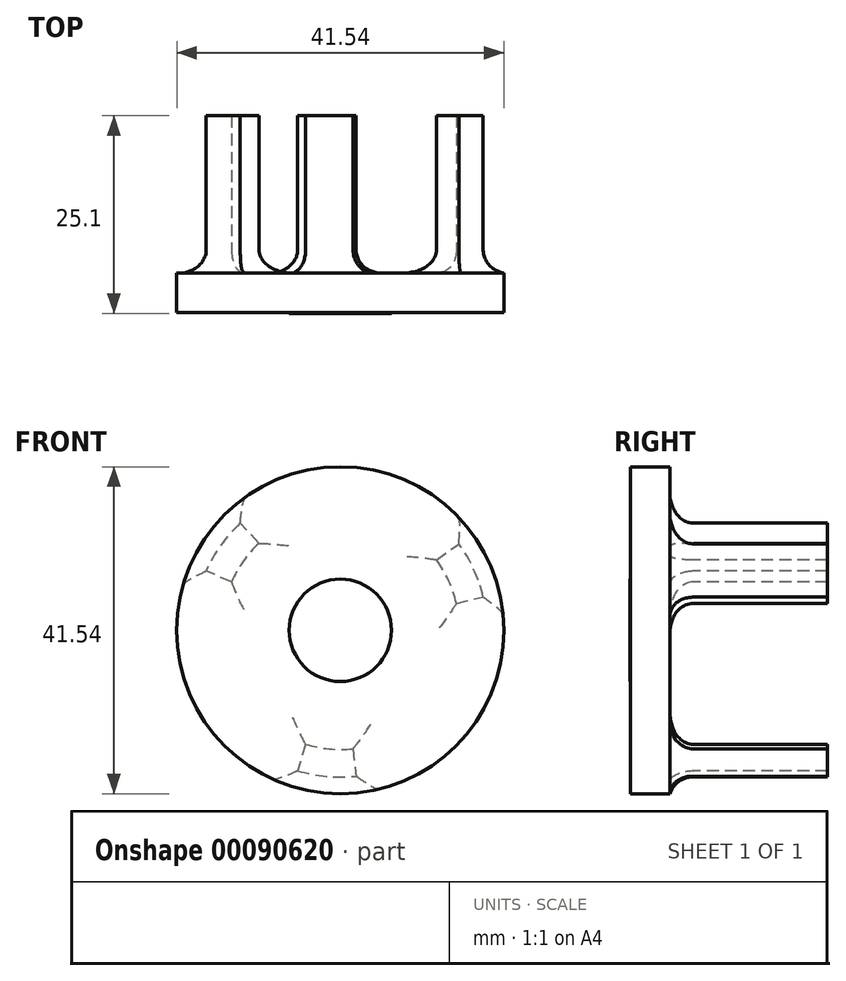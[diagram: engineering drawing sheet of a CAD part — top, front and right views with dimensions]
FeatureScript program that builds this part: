
annotation { "Feature Type Name" : "Feature", "Feature Type Description" : "" }
export const myFeature = defineFeature(function(context is Context, id is Id, definition is map)
    precondition{}
    {
        {
            var Q0;
            Q0=qCreatedBy(makeId("Front.planeOp"),FACE);
            var sketch = newSketch(context, id + "F0", { "sketchPlane" : qUnion([Q0])});
            skCircle(sketch, "E0", {"center": v(0, 0) * mm, "radius": 6.5 * mm});
            skSolve(sketch);
        }
        {
            var Q0;
            Q0=qSketchRegion(id+"F0",true);
            extrude(context, id + "F1", {"entities" : qUnion([Q0]), "depth" : .1 * mm});
        }
        {
            var Q0;
            Q0=qCreatedBy(makeId("Front.planeOp"),FACE);
            var sketch = newSketch(context, id + "F2", { "sketchPlane" : qUnion([Q0])});
            skCircle(sketch, "E1", {"center": v(0, 0) * mm, "radius": 20.77 * mm});
            skSolve(sketch);
        }
        {
            var Q0;
            Q0=makeQuery(id+"F2.imprint","IMPRINT",FACE,{"disambiguationData":[TD([[makeQuery(id+"F2.imprint","IMPRINT",EDGE,{"derivedFrom":sQuery(id+"F2.wireOp",EDGE,"E1")}),1.0]])]});
            extrude(context, id + "F3", {"entities" : qUnion([Q0]), "operationType" : NewBodyOperationType.ADD, "oppositeDirection" : true, "depth" : 5 * mm});
        }
        {
            var Q0;
            Q0=makeQuery(id+"F3.opExtrude","CAP_FACE",FACE,{"disambiguationData":[OSD([sQuery(id+"F2.wireOp",EDGE,"E1")])],"isStart":true});
            var sketch = newSketch(context, id + "F4", { "sketchPlane" : qUnion([Q0])});
            skCircle(sketch, "E2", {"center": v(0, 0) * mm, "radius": 18.64 * mm});
            skCircle(sketch, "E3", {"center": v(0, 0) * mm, "radius": 15.14 * mm});
            skLineSegment(sketch, "E4", {"start": v(0, 0) * mm, "end": v(-14.2, 15.17) * mm});
            skLineSegment(sketch, "E5", {"start": v(0, 0) * mm, "end": v(-19, 8.42) * mm});
            skLineSegment(sketch, "E6", {"start": v(0, 0) * mm, "end": v(16.79, 12.24) * mm});
            skLineSegment(sketch, "E7", {"start": v(0, 0) * mm, "end": v(20.23, 4.7) * mm});
            skLineSegment(sketch, "E8", {"start": v(0, 0) * mm, "end": v(-6.04, -19.88) * mm});
            skLineSegment(sketch, "E9", {"start": v(0, 0) * mm, "end": v(2.2, -20.66) * mm});
            skSolve(sketch);
        }
        {
            var Q0;
            {var subQ0=sQuery(id+"F4.wireOp",EDGE,"E4");var subQ1=sQuery(id+"F4.wireOp",EDGE,"E2");var subQ2=makeQuery(id+"F4.imprint","INTERSECT",VERTEX,{"derivedFrom":[subQ1,subQ0]});Q0=makeQuery(id+"F4.imprint","IMPRINT",FACE,{"disambiguationData":[TD([[makeQuery(id+"F4.imprint","IMPRINT",EDGE,{"disambiguationData":[TD([[subQ2,-1.0]])],"derivedFrom":subQ1}),1.0]])]});}
            var Q1;
            {var subQ0=sQuery(id+"F4.wireOp",EDGE,"E6");var subQ1=sQuery(id+"F4.wireOp",EDGE,"E2");var subQ2=makeQuery(id+"F4.imprint","INTERSECT",VERTEX,{"derivedFrom":[subQ1,subQ0]});Q1=makeQuery(id+"F4.imprint","IMPRINT",FACE,{"disambiguationData":[TD([[makeQuery(id+"F4.imprint","IMPRINT",EDGE,{"disambiguationData":[TD([[subQ2,1.0]])],"derivedFrom":subQ1}),1.0]])]});}
            var Q2;
            {var subQ0=sQuery(id+"F4.wireOp",EDGE,"E8");var subQ1=sQuery(id+"F4.wireOp",EDGE,"E2");var subQ2=makeQuery(id+"F4.imprint","INTERSECT",VERTEX,{"derivedFrom":[subQ1,subQ0]});Q2=makeQuery(id+"F4.imprint","IMPRINT",FACE,{"disambiguationData":[TD([[makeQuery(id+"F4.imprint","IMPRINT",EDGE,{"disambiguationData":[TD([[subQ2,-1.0]])],"derivedFrom":subQ1}),1.0]])]});}
            extrude(context, id + "F5", {"entities" : qUnion([Q0, Q1, Q2]), "operationType" : NewBodyOperationType.ADD, "oppositeDirection" : true, "depth" : 25 * mm});
        }
        {
            var Q0;
            Q0=makeQuery(id+"F5.boolean.opBoolean","INTERSECT",EDGE,{"derivedFrom":[makeQuery(id+"F3.opExtrude","CAP_FACE",FACE,{"disambiguationData":[OSD([sQuery(id+"F2.wireOp",EDGE,"E1")])],"isStart":false}),makeQuery(id+"F5.opExtrude","SWEPT_FACE",FACE,{"disambiguationData":[OSD([sQuery(id+"F4.wireOp",EDGE,"E5")])]})]});
            var Q1;
            {var subQ0=sQuery(id+"F4.wireOp",EDGE,"E3");Q1=makeQuery(id+"F5.boolean.opBoolean","INTERSECT",EDGE,{"derivedFrom":[makeQuery(id+"F3.opExtrude","CAP_FACE",FACE,{"disambiguationData":[OSD([sQuery(id+"F2.wireOp",EDGE,"E1")])],"isStart":false}),makeQuery(id+"F5.opExtrude","SWEPT_FACE",FACE,{"disambiguationData":[OSD([subQ0]),TDD([makeQuery(id+"F4.imprint","IMPRINT",EDGE,{"disambiguationData":[TD([[makeQuery(id+"F4.imprint","INTERSECT",VERTEX,{"derivedFrom":[subQ0,sQuery(id+"F4.wireOp",EDGE,"E4")]}),-1.0]])],"derivedFrom":subQ0})])]})]});}
            var Q2;
            Q2=makeQuery(id+"F5.boolean.opBoolean","INTERSECT",EDGE,{"derivedFrom":[makeQuery(id+"F3.opExtrude","CAP_FACE",FACE,{"disambiguationData":[OSD([sQuery(id+"F2.wireOp",EDGE,"E1")])],"isStart":false}),makeQuery(id+"F5.opExtrude","SWEPT_FACE",FACE,{"disambiguationData":[OSD([sQuery(id+"F4.wireOp",EDGE,"E4")])]})]});
            var Q3;
            {var subQ0=sQuery(id+"F4.wireOp",EDGE,"E2");Q3=makeQuery(id+"F5.boolean.opBoolean","INTERSECT",EDGE,{"derivedFrom":[makeQuery(id+"F3.opExtrude","CAP_FACE",FACE,{"disambiguationData":[OSD([sQuery(id+"F2.wireOp",EDGE,"E1")])],"isStart":false}),makeQuery(id+"F5.opExtrude","SWEPT_FACE",FACE,{"disambiguationData":[OSD([subQ0]),TDD([makeQuery(id+"F4.imprint","IMPRINT",EDGE,{"disambiguationData":[TD([[makeQuery(id+"F4.imprint","INTERSECT",VERTEX,{"derivedFrom":[subQ0,sQuery(id+"F4.wireOp",EDGE,"E4")]}),-1.0]])],"derivedFrom":subQ0})])]})]});}
            var Q4;
            {var subQ0=sQuery(id+"F4.wireOp",EDGE,"E2");Q4=makeQuery(id+"F5.boolean.opBoolean","INTERSECT",EDGE,{"derivedFrom":[makeQuery(id+"F3.opExtrude","CAP_FACE",FACE,{"disambiguationData":[OSD([sQuery(id+"F2.wireOp",EDGE,"E1")])],"isStart":false}),makeQuery(id+"F5.opExtrude","SWEPT_FACE",FACE,{"disambiguationData":[OSD([subQ0]),TDD([makeQuery(id+"F4.imprint","IMPRINT",EDGE,{"disambiguationData":[TD([[makeQuery(id+"F4.imprint","INTERSECT",VERTEX,{"derivedFrom":[subQ0,sQuery(id+"F4.wireOp",EDGE,"E6")]}),1.0]])],"derivedFrom":subQ0})])]})]});}
            var Q5;
            Q5=makeQuery(id+"F5.boolean.opBoolean","INTERSECT",EDGE,{"derivedFrom":[makeQuery(id+"F3.opExtrude","CAP_FACE",FACE,{"disambiguationData":[OSD([sQuery(id+"F2.wireOp",EDGE,"E1")])],"isStart":false}),makeQuery(id+"F5.opExtrude","SWEPT_FACE",FACE,{"disambiguationData":[OSD([sQuery(id+"F4.wireOp",EDGE,"E6")])]})]});
            var Q6;
            {var subQ0=sQuery(id+"F4.wireOp",EDGE,"E3");Q6=makeQuery(id+"F5.boolean.opBoolean","INTERSECT",EDGE,{"derivedFrom":[makeQuery(id+"F3.opExtrude","CAP_FACE",FACE,{"disambiguationData":[OSD([sQuery(id+"F2.wireOp",EDGE,"E1")])],"isStart":false}),makeQuery(id+"F5.opExtrude","SWEPT_FACE",FACE,{"disambiguationData":[OSD([subQ0]),TDD([makeQuery(id+"F4.imprint","IMPRINT",EDGE,{"disambiguationData":[TD([[makeQuery(id+"F4.imprint","INTERSECT",VERTEX,{"derivedFrom":[subQ0,sQuery(id+"F4.wireOp",EDGE,"E6")]}),1.0]])],"derivedFrom":subQ0})])]})]});}
            var Q7;
            Q7=makeQuery(id+"F5.boolean.opBoolean","INTERSECT",EDGE,{"derivedFrom":[makeQuery(id+"F3.opExtrude","CAP_FACE",FACE,{"disambiguationData":[OSD([sQuery(id+"F2.wireOp",EDGE,"E1")])],"isStart":false}),makeQuery(id+"F5.opExtrude","SWEPT_FACE",FACE,{"disambiguationData":[OSD([sQuery(id+"F4.wireOp",EDGE,"E7")])]})]});
            var Q8;
            {var subQ0=sQuery(id+"F4.wireOp",EDGE,"E2");Q8=makeQuery(id+"F5.boolean.opBoolean","INTERSECT",EDGE,{"derivedFrom":[makeQuery(id+"F3.opExtrude","CAP_FACE",FACE,{"disambiguationData":[OSD([sQuery(id+"F2.wireOp",EDGE,"E1")])],"isStart":false}),makeQuery(id+"F5.opExtrude","SWEPT_FACE",FACE,{"disambiguationData":[OSD([subQ0]),TDD([makeQuery(id+"F4.imprint","IMPRINT",EDGE,{"disambiguationData":[TD([[makeQuery(id+"F4.imprint","INTERSECT",VERTEX,{"derivedFrom":[subQ0,sQuery(id+"F4.wireOp",EDGE,"E8")]}),-1.0]])],"derivedFrom":subQ0})])]})]});}
            var Q9;
            Q9=makeQuery(id+"F5.boolean.opBoolean","INTERSECT",EDGE,{"derivedFrom":[makeQuery(id+"F3.opExtrude","CAP_FACE",FACE,{"disambiguationData":[OSD([sQuery(id+"F2.wireOp",EDGE,"E1")])],"isStart":false}),makeQuery(id+"F5.opExtrude","SWEPT_FACE",FACE,{"disambiguationData":[OSD([sQuery(id+"F4.wireOp",EDGE,"E8")])]})]});
            var Q10;
            {var subQ0=sQuery(id+"F4.wireOp",EDGE,"E3");Q10=makeQuery(id+"F5.boolean.opBoolean","INTERSECT",EDGE,{"derivedFrom":[makeQuery(id+"F3.opExtrude","CAP_FACE",FACE,{"disambiguationData":[OSD([sQuery(id+"F2.wireOp",EDGE,"E1")])],"isStart":false}),makeQuery(id+"F5.opExtrude","SWEPT_FACE",FACE,{"disambiguationData":[OSD([subQ0]),TDD([makeQuery(id+"F4.imprint","IMPRINT",EDGE,{"disambiguationData":[TD([[makeQuery(id+"F4.imprint","INTERSECT",VERTEX,{"derivedFrom":[subQ0,sQuery(id+"F4.wireOp",EDGE,"E8")]}),-1.0]])],"derivedFrom":subQ0})])]})]});}
            var Q11;
            Q11=makeQuery(id+"F5.boolean.opBoolean","INTERSECT",EDGE,{"derivedFrom":[makeQuery(id+"F3.opExtrude","CAP_FACE",FACE,{"disambiguationData":[OSD([sQuery(id+"F2.wireOp",EDGE,"E1")])],"isStart":false}),makeQuery(id+"F5.opExtrude","SWEPT_FACE",FACE,{"disambiguationData":[OSD([sQuery(id+"F4.wireOp",EDGE,"E9")])]})]});
            fillet(context, id + "F6", {"entities" : qUnion([Q0, Q1, Q2, Q3, Q4, Q5, Q6, Q7, Q8, Q9, Q10, Q11]), "radius" : 3 * mm, "tangentPropagation" : true, "allowEdgeOverflow" : false});
        }
    });
